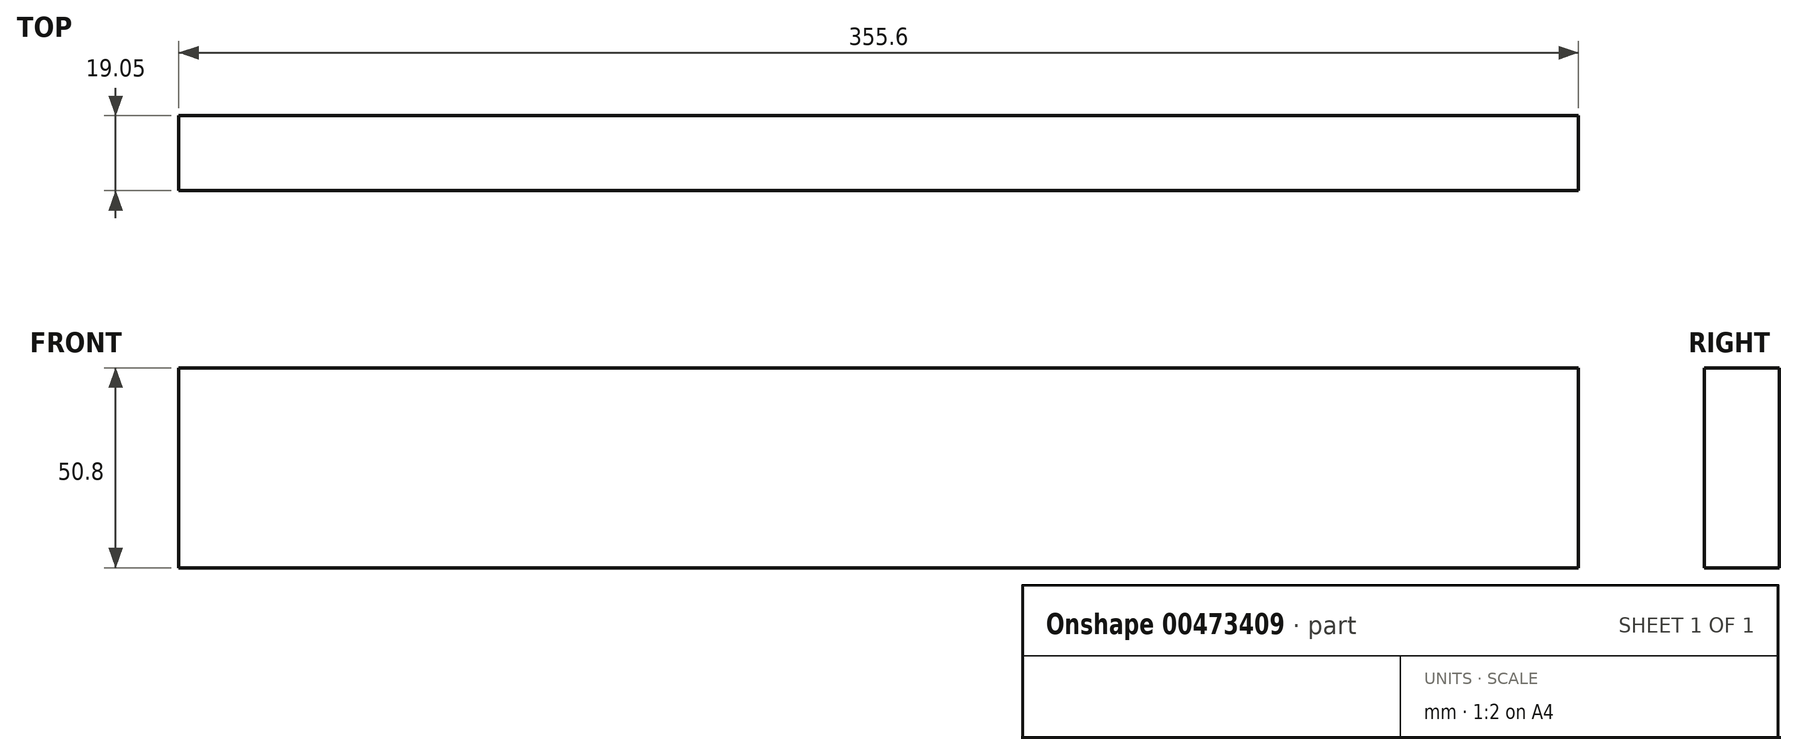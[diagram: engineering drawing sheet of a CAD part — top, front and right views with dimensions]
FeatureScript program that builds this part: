
annotation { "Feature Type Name" : "Feature", "Feature Type Description" : "" }
export const myFeature = defineFeature(function(context is Context, id is Id, definition is map)
    precondition{}
    {
        {
            var Q0;
            Q0=qCreatedBy(makeId("Front.planeOp"),FACE);
            var sketch = newSketch(context, id + "F0", { "sketchPlane" : qUnion([Q0])});
            skLineSegment(sketch, "E0.bottom", {"start": v(14.4, 54.83) * mm, "end": v(370, 54.83) * mm});
            skLineSegment(sketch, "E0.top", {"start": v(14.4, 4.03) * mm, "end": v(370, 4.03) * mm});
            skLineSegment(sketch, "E0.left", {"start": v(14.4, 54.83) * mm, "end": v(14.4, 4.03) * mm});
            skLineSegment(sketch, "E0.right", {"start": v(370, 54.83) * mm, "end": v(370, 4.03) * mm});
            skSolve(sketch);
        }
        {
            var Q0;
            Q0=makeQuery(id+"F0.imprint","IMPRINT",FACE,{"disambiguationData":[TD([[makeQuery(id+"F0.imprint","IMPRINT",EDGE,{"derivedFrom":sQuery(id+"F0.wireOp",EDGE,"E0.bottom")}),-1.0]])]});
            extrude(context, id + "F1", {"entities" : qUnion([Q0]), "depth" : 19.05 * mm});
        }
    });
